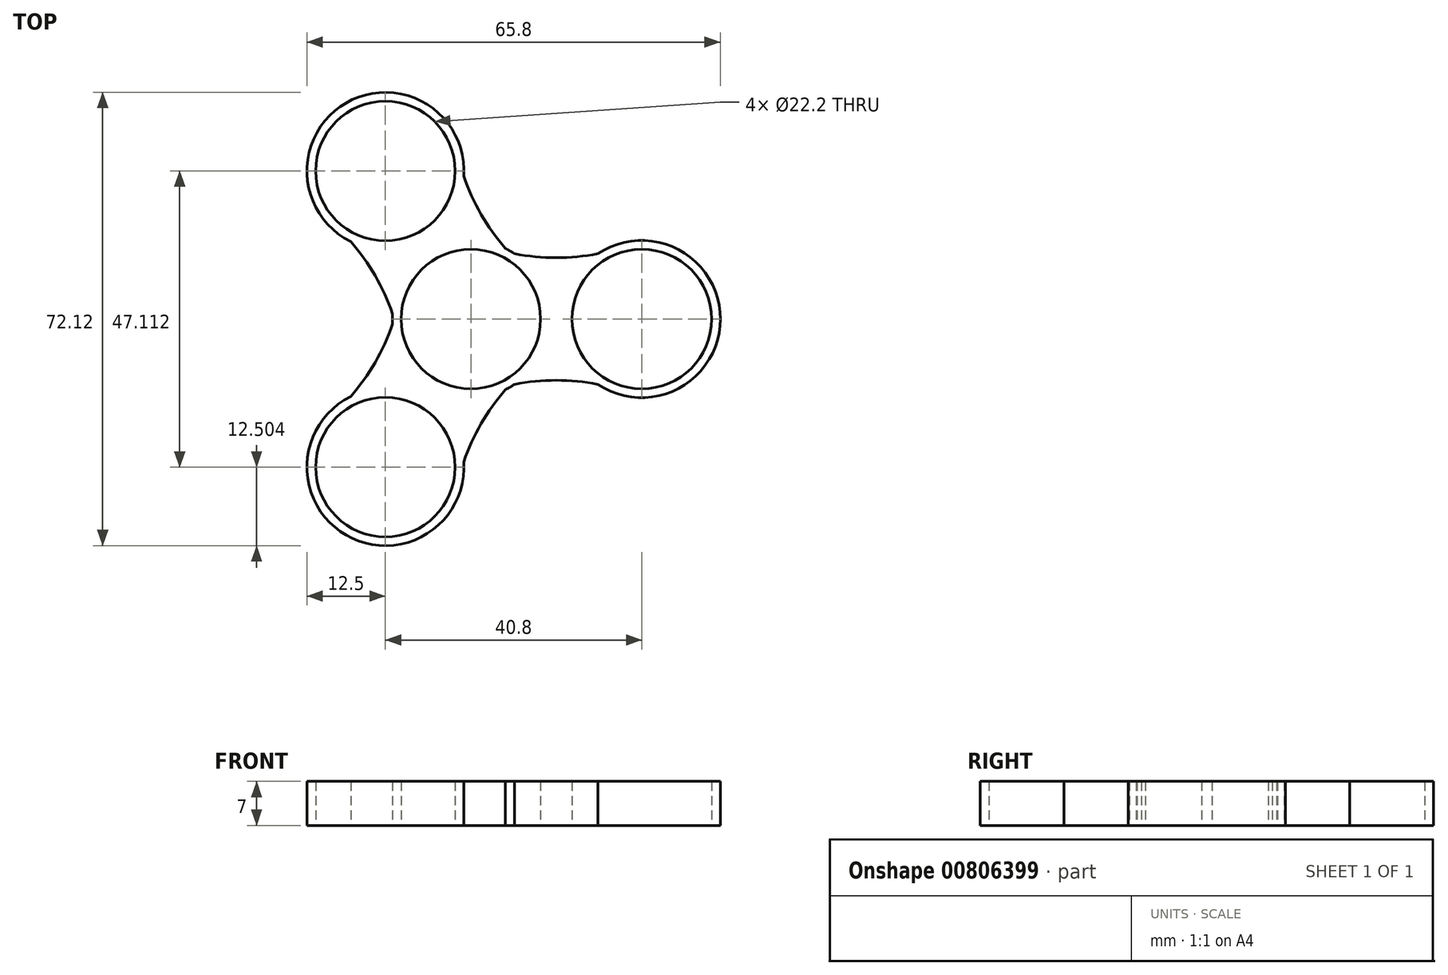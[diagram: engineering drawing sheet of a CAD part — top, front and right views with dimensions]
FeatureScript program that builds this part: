
annotation { "Feature Type Name" : "Feature", "Feature Type Description" : "" }
export const myFeature = defineFeature(function(context is Context, id is Id, definition is map)
    precondition{}
    {
        {
            var Q0;
            Q0=qCreatedBy(makeId("Top.planeOp"),FACE);
            var sketch = newSketch(context, id + "F0", { "sketchPlane" : qUnion([Q0])});
            skPoint(sketch, "E0", {"position": v(-7.9, 10.77) * mm});
            skPoint(sketch, "E1.end.orphan", {"position": v(-5.55, 0) * mm});
            skPoint(sketch, "E2.start.orphan", {"position": v(0, 0) * mm});
            skPoint(sketch, "E3.end.orphan", {"position": v(-11.1, 0) * mm});
            skCircle(sketch, "E4", {"center": v(0, 0) * mm, "radius": 11.1 * mm});
            skPoint(sketch, "E5.first.point", {"position": v(37.63, -29.52) * mm});
            skPoint(sketch, "E5.second.point", {"position": v(25.4, -27.02) * mm});
            skPoint(sketch, "E5.third.point", {"position": v(25.65, -35) * mm});
            skPoint(sketch, "E6.start.orphan", {"position": v(11.1, 0) * mm});
            skPoint(sketch, "E7.second.point", {"position": v(47.11, 7.68) * mm});
            skPoint(sketch, "E7.third.point", {"position": v(47.11, 7.92) * mm});
            skArc(sketch, "E8.trimOffspring", {"start": v(47.11, 7.68) * mm, "mid": v(47.11, 7.8) * mm, "end": v(47.11, 7.92) * mm});
            skCircle(sketch, "E9", {"center": v(0, 0) * mm, "radius": 12.5 * mm});
            skLineSegment(sketch, "E10", {"start": v(11.1, 0) * mm, "end": v(16.1, 0) * mm});
            skLineSegment(sketch, "E11", {"start": v(16.1, 0) * mm, "end": v(27.2, 0) * mm});
            skCircle(sketch, "E12", {"center": v(27.2, 0) * mm, "radius": 11.1 * mm});
            skCircle(sketch, "E13", {"center": v(27.2, 0) * mm, "radius": 12.5 * mm});
            skArc(sketch, "E14", {"start": v(6.96, 10.39) * mm, "mid": v(13.6, 9.75) * mm, "end": v(20.24, 10.39) * mm});
            skArc(sketch, "E15", {"start": v(20.24, -10.39) * mm, "mid": v(13.6, -9.75) * mm, "end": v(6.96, -10.39) * mm});
            skCircle(sketch, "E16.1.0", {"center": v(-13.6, 23.56) * mm, "radius": 11.1 * mm});
            skCircle(sketch, "E16.1.1", {"center": v(-13.6, 23.56) * mm, "radius": 12.5 * mm});
            skArc(sketch, "E16.1.2", {"start": v(-12.47, 0.83) * mm, "mid": v(-15.24, 6.9) * mm, "end": v(-19.12, 12.34) * mm});
            skArc(sketch, "E16.1.3", {"start": v(-1.13, 22.73) * mm, "mid": v(1.64, 16.65) * mm, "end": v(5.52, 11.22) * mm});
            skCircle(sketch, "E16.2.0", {"center": v(-13.6, -23.56) * mm, "radius": 11.1 * mm});
            skCircle(sketch, "E16.2.1", {"center": v(-13.6, -23.56) * mm, "radius": 12.5 * mm});
            skArc(sketch, "E16.2.2", {"start": v(5.52, -11.22) * mm, "mid": v(1.64, -16.65) * mm, "end": v(-1.13, -22.73) * mm});
            skArc(sketch, "E16.2.3", {"start": v(-19.12, -12.34) * mm, "mid": v(-15.24, -6.9) * mm, "end": v(-12.47, -0.83) * mm});
            skPoint(sketch, "E17.orphan", {"position": v(27.2, 12.5) * mm});
            skPoint(sketch, "E18.orphan", {"position": v(0, 12.5) * mm});
            skPoint(sketch, "E19.orphan", {"position": v(10.83, 6.25) * mm});
            skPoint(sketch, "E20.orphan", {"position": v(10.83, -6.25) * mm});
            skPoint(sketch, "E21.orphan", {"position": v(0, -12.5) * mm});
            skPoint(sketch, "E22.orphan", {"position": v(27.2, -12.5) * mm});
            skPoint(sketch, "E23.orphan", {"position": v(-2.77, -29.8) * mm});
            skPoint(sketch, "E24.orphan", {"position": v(-24.43, -17.3) * mm});
            skPoint(sketch, "E25.orphan", {"position": v(-24.43, 17.3) * mm});
            skPoint(sketch, "E26.orphan", {"position": v(-2.77, 29.8) * mm});
            skPoint(sketch, "E27.orphan", {"position": v(-10.83, -6.25) * mm});
            skPoint(sketch, "E28.orphan", {"position": v(-10.83, 6.25) * mm});
            skSolve(sketch);
        }
        {
            var Q0;
            Q0 = qSketchRegion(id + "F0", true);
            extrude(context, id + "F1", {"entities" : qUnion([Q0]), "depth" : 7 * mm, "offsetDistance" : 25 * mm});
        }
    });
